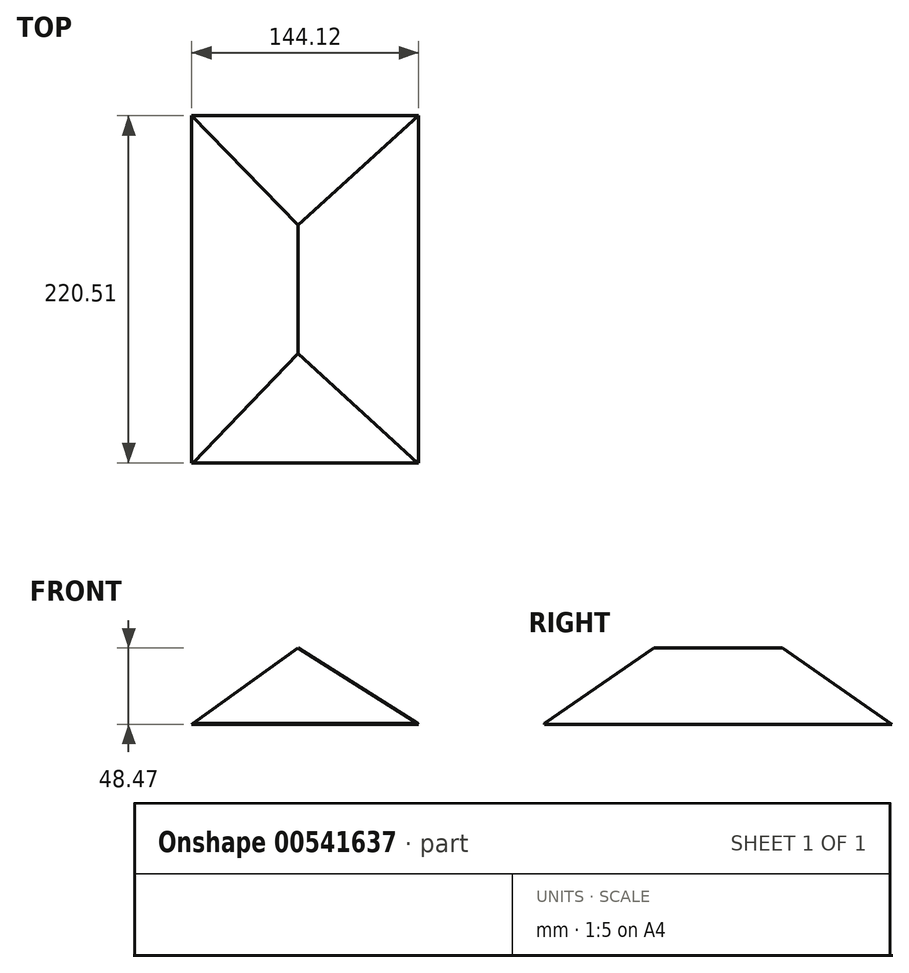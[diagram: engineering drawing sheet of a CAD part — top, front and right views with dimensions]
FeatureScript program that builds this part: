
annotation { "Feature Type Name" : "Feature", "Feature Type Description" : "" }
export const myFeature = defineFeature(function(context is Context, id is Id, definition is map)
    precondition{}
    {
        {
            var Q0;
            Q0=qCreatedBy(makeId("Front.planeOp"),FACE);
            var sketch = newSketch(context, id + "F0", { "sketchPlane" : qUnion([Q0])});
            skLineSegment(sketch, "E0", {"start": v(76.82, 120.86) * mm, "end": v(220.94, 120.86) * mm});
            skLineSegment(sketch, "E1", {"start": v(220.94, 120.86) * mm, "end": v(144.42, 169.33) * mm});
            skLineSegment(sketch, "E2", {"start": v(144.42, 169.33) * mm, "end": v(76.82, 120.86) * mm});
            skSolve(sketch);
        }
        {
            var Q0;
            Q0=makeQuery(id+"F0.imprint","IMPRINT",FACE,{"disambiguationData":[TD([[makeQuery(id+"F0.imprint","IMPRINT",EDGE,{"derivedFrom":sQuery(id+"F0.wireOp",EDGE,"E0")}),1.0]])]});
            extrude(context, id + "F1", {"entities" : qUnion([Q0]), "oppositeDirection" : true, "depth" : 221.5 * mm, "offsetDistance" : 25.4 * mm});
        }
        {
            var Q0;
            Q0=qCreatedBy(makeId("Right.planeOp"),FACE);
            var sketch = newSketch(context, id + "F2", { "sketchPlane" : qUnion([Q0])});
            skLineSegment(sketch, "E3", {"start": v(0, 121.4) * mm, "end": v(78.75, 175.77) * mm});
            skLineSegment(sketch, "E4", {"start": v(78.75, 175.77) * mm, "end": v(-13.19, 175.77) * mm});
            skLineSegment(sketch, "E5", {"start": v(-13.19, 175.77) * mm, "end": v(-13.19, 115.6) * mm});
            skLineSegment(sketch, "E6", {"start": v(-13.19, 115.6) * mm, "end": v(0, 121.4) * mm});
            skSolve(sketch);
        }
        {
            var Q0;
            Q0=makeQuery(id+"F2.imprint","IMPRINT",FACE,{"disambiguationData":[TD([[makeQuery(id+"F2.imprint","IMPRINT",EDGE,{"derivedFrom":sQuery(id+"F2.wireOp",EDGE,"E3")}),1.0]])]});
            extrude(context, id + "F3", {"entities" : qUnion([Q0]), "operationType" : NewBodyOperationType.REMOVE, "depth" : 383.8 * mm, "offsetDistance" : 25.4 * mm});
        }
        {
            var Q0;
            Q0=qCreatedBy(makeId("Right.planeOp"),FACE);
            var sketch = newSketch(context, id + "F4", { "sketchPlane" : qUnion([Q0])});
            skLineSegment(sketch, "E7", {"start": v(223.23, 118.96) * mm, "end": v(141.07, 176.38) * mm});
            skLineSegment(sketch, "E8", {"start": v(141.07, 176.38) * mm, "end": v(241.26, 179.13) * mm});
            skLineSegment(sketch, "E9", {"start": v(241.26, 179.13) * mm, "end": v(241.26, 92.69) * mm});
            skLineSegment(sketch, "E10", {"start": v(241.26, 92.69) * mm, "end": v(223.23, 118.96) * mm});
            skSolve(sketch);
        }
        {
            var Q0;
            Q0 = qSketchRegion(id + "F4", true);
            extrude(context, id + "F5", {"entities" : qUnion([Q0]), "operationType" : NewBodyOperationType.REMOVE, "depth" : 385.06 * mm, "offsetDistance" : 25.4 * mm});
        }
    });
